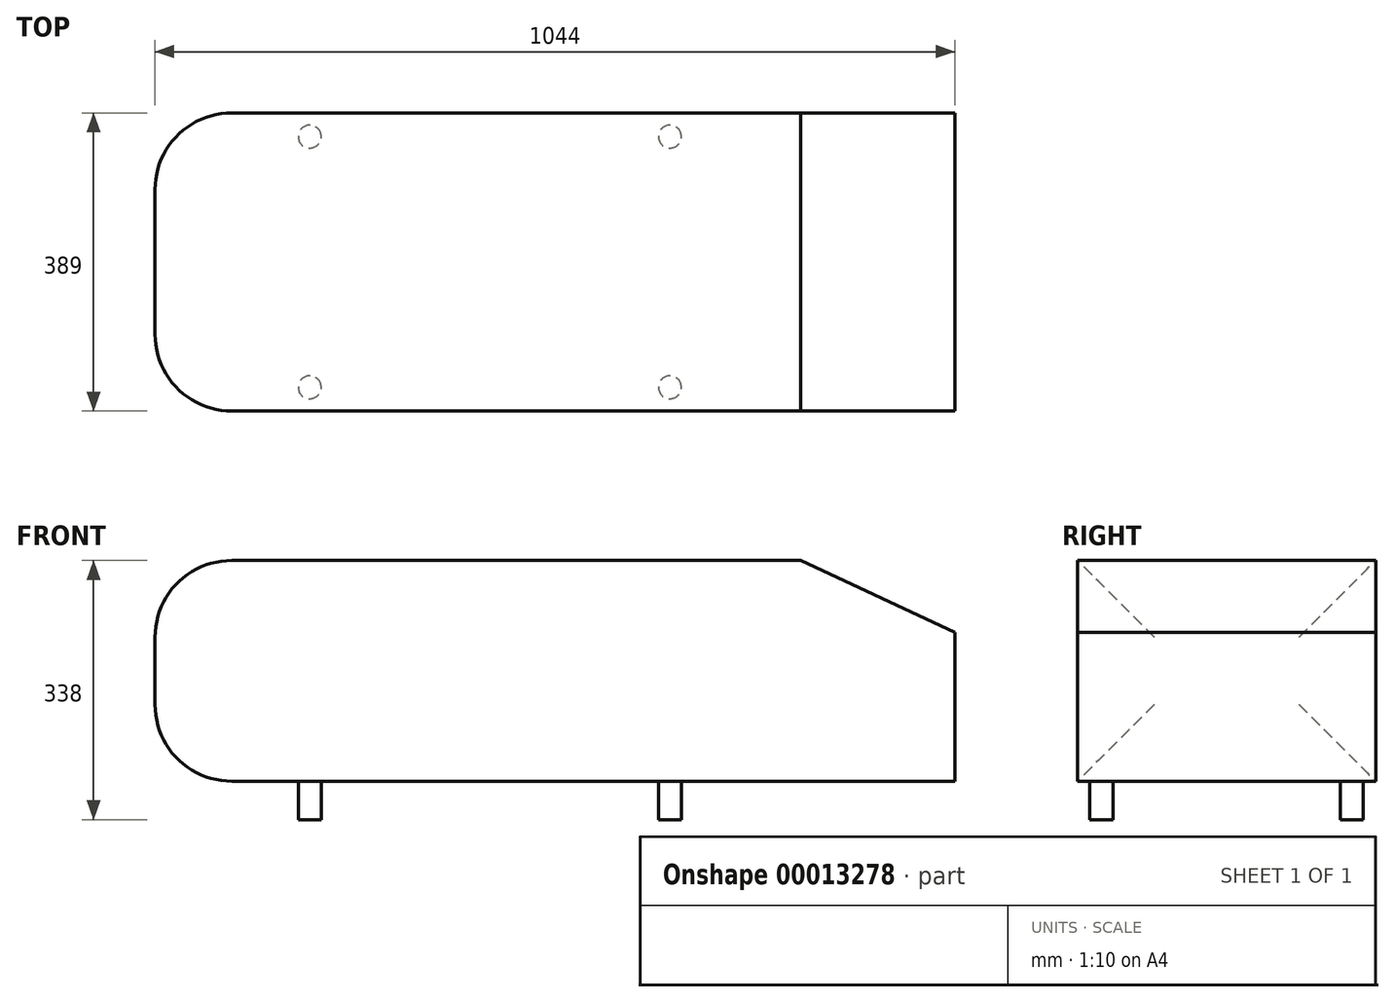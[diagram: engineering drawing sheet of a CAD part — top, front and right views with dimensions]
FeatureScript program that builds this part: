
annotation { "Feature Type Name" : "Feature", "Feature Type Description" : "" }
export const myFeature = defineFeature(function(context is Context, id is Id, definition is map)
    precondition{}
    {
        {
            var Q0;
            Q0=qCreatedBy(makeId("Top.planeOp"),FACE);
            var sketch = newSketch(context, id + "F0", { "sketchPlane" : qUnion([Q0])});
            skLineSegment(sketch, "E0.rect.bottom", {"start": v(-522, 194.5) * mm, "end": v(522, 194.5) * mm});
            skLineSegment(sketch, "E0.rect.top", {"start": v(-522, -194.5) * mm, "end": v(522, -194.5) * mm});
            skLineSegment(sketch, "E0.rect.left", {"start": v(-522, 194.5) * mm, "end": v(-522, -194.5) * mm});
            skLineSegment(sketch, "E0.rect.right", {"start": v(522, 194.5) * mm, "end": v(522, -194.5) * mm});
            skPoint(sketch, "E0.rect.middle", {"position": v(0, 0) * mm});
            skCircle(sketch, "E1", {"center": v(-320, -163.5) * mm, "radius": 15 * mm});
            skLineSegment(sketch, "E2", {"start": v(-522, 0) * mm, "end": v(522, 0) * mm});
            skCircle(sketch, "E3", {"center": v(-320, 163.5) * mm, "radius": 15 * mm});
            skCircle(sketch, "E4", {"center": v(150, 163.5) * mm, "radius": 15 * mm});
            skCircle(sketch, "E5", {"center": v(150, -163.5) * mm, "radius": 15 * mm});
            skSolve(sketch);
        }
        {
            var Q0;
            Q0=makeQuery(id+"F0.imprint","IMPRINT",FACE,{"disambiguationData":[TD([[makeQuery(id+"F0.imprint","IMPRINT",EDGE,{"derivedFrom":sQuery(id+"F0.wireOp",EDGE,"E1")}),1.0]])]});
            var Q1;
            Q1=makeQuery(id+"F0.imprint","IMPRINT",FACE,{"disambiguationData":[TD([[makeQuery(id+"F0.imprint","IMPRINT",EDGE,{"derivedFrom":sQuery(id+"F0.wireOp",EDGE,"E5")}),1.0]])]});
            var Q2;
            Q2=makeQuery(id+"F0.imprint","IMPRINT",FACE,{"disambiguationData":[TD([[makeQuery(id+"F0.imprint","IMPRINT",EDGE,{"derivedFrom":sQuery(id+"F0.wireOp",EDGE,"E4")}),1.0]])]});
            var Q3;
            Q3=makeQuery(id+"F0.imprint","IMPRINT",FACE,{"disambiguationData":[TD([[makeQuery(id+"F0.imprint","IMPRINT",EDGE,{"derivedFrom":sQuery(id+"F0.wireOp",EDGE,"E3")}),1.0]])]});
            extrude(context, id + "F1", {"entities" : qUnion([Q0, Q1, Q2, Q3]), "oppositeDirection" : true, "depth" : 50 * mm});
        }
        {
            var Q0;
            {var subQ2=sQuery(id+"F0.wireOp",EDGE,"E0.rect.bottom");Q0=makeQuery(id+"F0.imprint","IMPRINT",FACE,{"disambiguationData":[TD([[makeQuery(id+"F0.imprint","IMPRINT",EDGE,{"derivedFrom":subQ2}),-1.0]])]});}
            var Q1;
            {var subQ2=sQuery(id+"F0.wireOp",EDGE,"E0.rect.top");Q1=makeQuery(id+"F0.imprint","IMPRINT",FACE,{"disambiguationData":[TD([[makeQuery(id+"F0.imprint","IMPRINT",EDGE,{"derivedFrom":subQ2}),1.0]])]});}
            var Q2;
            Q2=makeQuery(id+"F0.imprint","IMPRINT",FACE,{"disambiguationData":[TD([[makeQuery(id+"F0.imprint","IMPRINT",EDGE,{"derivedFrom":sQuery(id+"F0.wireOp",EDGE,"E4")}),1.0]])]});
            var Q3;
            Q3=makeQuery(id+"F0.imprint","IMPRINT",FACE,{"disambiguationData":[TD([[makeQuery(id+"F0.imprint","IMPRINT",EDGE,{"derivedFrom":sQuery(id+"F0.wireOp",EDGE,"E3")}),1.0]])]});
            var Q4;
            Q4=makeQuery(id+"F0.imprint","IMPRINT",FACE,{"disambiguationData":[TD([[makeQuery(id+"F0.imprint","IMPRINT",EDGE,{"derivedFrom":sQuery(id+"F0.wireOp",EDGE,"E1")}),1.0]])]});
            var Q5;
            Q5=makeQuery(id+"F0.imprint","IMPRINT",FACE,{"disambiguationData":[TD([[makeQuery(id+"F0.imprint","IMPRINT",EDGE,{"derivedFrom":sQuery(id+"F0.wireOp",EDGE,"E5")}),1.0]])]});
            extrude(context, id + "F2", {"entities" : qUnion([Q0, Q1, Q2, Q3, Q4, Q5]), "depth" : 288 * mm, "offsetDistance" : 25 * mm});
        }
        {
            var Q0;
            Q0=makeQuery(id+"F2.opExtrude","CAP_EDGE",EDGE,{"disambiguationData":[OSD([sQuery(id+"F0.wireOp",EDGE,"E0.rect.left")])],"isStart":false});
            var Q1;
            Q1=makeQuery(id+"F2.opExtrude","CAP_EDGE",EDGE,{"disambiguationData":[OSD([sQuery(id+"F0.wireOp",EDGE,"E0.rect.left")])],"isStart":true});
            var Q2;
            Q2=makeQuery(id+"F2.opExtrude","SWEPT_EDGE",EDGE,{"disambiguationData":[OSD([sQuery(id+"F0.wireOp",EDGE,"E0.rect.top"),sQuery(id+"F0.wireOp",EDGE,"E0.rect.left")])]});
            var Q3;
            Q3=makeQuery(id+"F2.opExtrude","SWEPT_EDGE",EDGE,{"disambiguationData":[OSD([sQuery(id+"F0.wireOp",EDGE,"E0.rect.bottom"),sQuery(id+"F0.wireOp",EDGE,"E0.rect.left")])]});
            fillet(context, id + "F3", {"entities" : qUnion([Q0, Q1, Q2, Q3]), "radius" : 100 * mm, "tangentPropagation" : true, "allowEdgeOverflow" : false});
        }
        {
            var Q0;
            Q0=makeQuery(id+"F2.opExtrude","SWEPT_FACE",FACE,{"disambiguationData":[OSD([sQuery(id+"F0.wireOp",EDGE,"E0.rect.top")])]});
            var sketch = newSketch(context, id + "F4", { "sketchPlane" : qUnion([Q0])});
            skLineSegment(sketch, "E6", {"start": v(320.8, 288) * mm, "end": v(522, 194.18) * mm});
            skSolve(sketch);
        }
        {
            var Q0;
            Q0 = qSketchRegion(id + "F4", true);
            var Q1;
            {var subQ2=sQuery(id+"F4.wireOp",EDGE,"E6");Q1=makeQuery(id+"F4.imprint","IMPRINT",FACE,{"disambiguationData":[TD([[makeQuery(id+"F4.imprint","IMPRINT",EDGE,{"derivedFrom":subQ2}),1.0]])]});}
            extrude(context, id + "F5", {"entities" : qUnion([Q0, Q1]), "operationType" : NewBodyOperationType.REMOVE, "endBound" : BoundingType.THROUGH_ALL, "oppositeDirection" : true, "depth" : 25 * mm});
        }
    });
